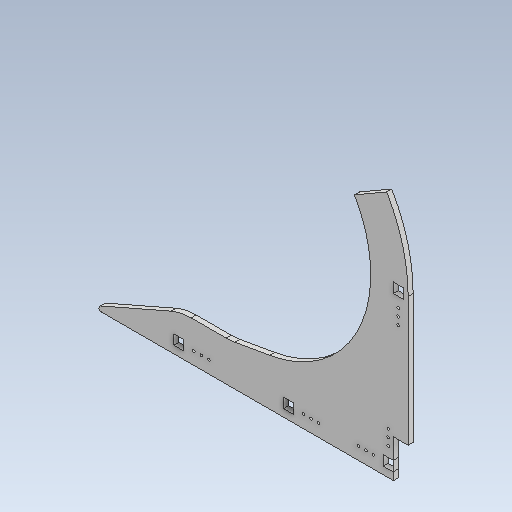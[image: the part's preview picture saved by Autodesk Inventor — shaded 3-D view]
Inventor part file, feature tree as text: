
AUTODESK INVENTOR PART (.ipt)
format: ipt  version: 2020 (Build 240168000, 168)  size: 158,720 bytes
history: native  units: in
note: dims shown in document units (in); Inventor stores cm internally (conversion verified against a paired STEP export)
features: other x3, sketch x1
ambient origin geometry x8: Origin, YZ Plane, XZ Plane, XY Plane, X Axis, Y Axis, Z Axis, Center Point
bodies: Solid1 (feature_tree)
feature tree (4):
  other  "OuterWheelIndexer.ipt"
  other  "Solid1::OuterWheelIndexer.ipt"
  other  "TaggingFeature1"
  sketch  "Sketch1"  dims[d0=0.3937in]
